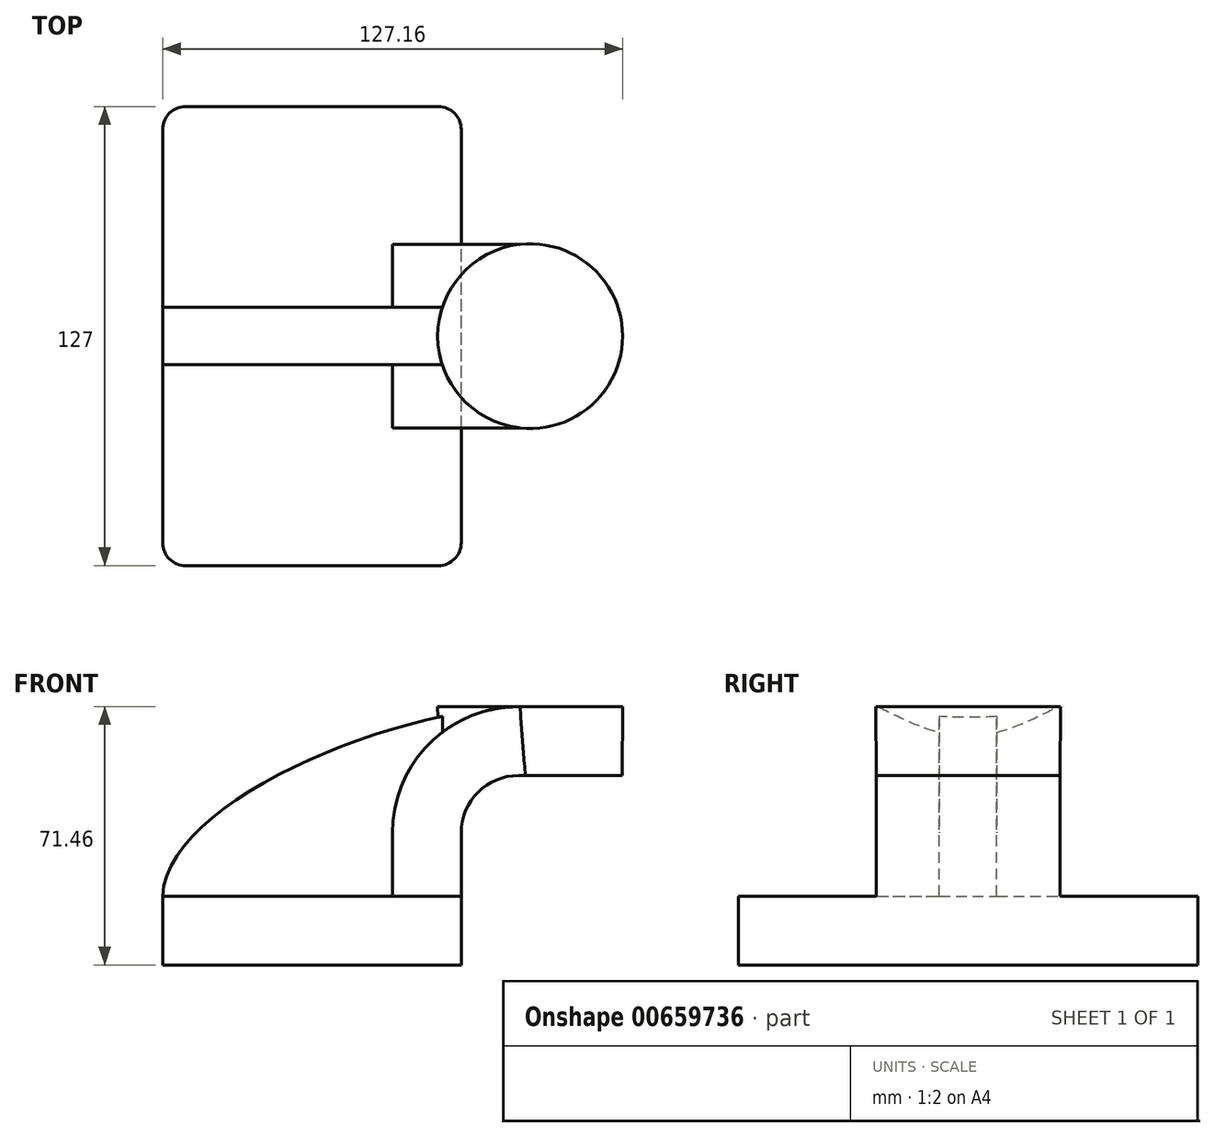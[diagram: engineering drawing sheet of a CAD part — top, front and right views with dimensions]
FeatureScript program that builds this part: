
annotation { "Feature Type Name" : "Feature", "Feature Type Description" : "" }
export const myFeature = defineFeature(function(context is Context, id is Id, definition is map)
    precondition{}
    {
        {
            var Q0;
            Q0=qCreatedBy(makeId("Front.planeOp"),FACE);
            var sketch = newSketch(context, id + "F0", { "sketchPlane" : qUnion([Q0])});
            skLineSegment(sketch, "E0.bottom", {"start": v(41.28, -9.52) * mm, "end": v(-41.28, -9.53) * mm});
            skLineSegment(sketch, "E0.top", {"start": v(41.28, 9.53) * mm, "end": v(-41.28, 9.53) * mm});
            skLineSegment(sketch, "E0.left", {"start": v(41.28, -9.52) * mm, "end": v(41.28, 9.53) * mm});
            skLineSegment(sketch, "E0.right", {"start": v(-41.28, -9.53) * mm, "end": v(-41.28, 9.53) * mm});
            skPoint(sketch, "E0.middle", {"position": v(0, 0) * mm});
            skLineSegment(sketch, "E1.bottom", {"start": v(111.12, 38.1) * mm, "end": v(60.32, 38.1) * mm});
            skLineSegment(sketch, "E1.top", {"start": v(111.12, 66.68) * mm, "end": v(60.32, 66.68) * mm});
            skLineSegment(sketch, "E1.left", {"start": v(111.12, 38.1) * mm, "end": v(111.12, 66.68) * mm});
            skLineSegment(sketch, "E1.right", {"start": v(60.32, 38.1) * mm, "end": v(60.32, 66.68) * mm});
            skPoint(sketch, "E1.middle", {"position": v(85.72, 52.39) * mm});
            skLineSegment(sketch, "E2", {"start": v(41.27, 9.53) * mm, "end": v(41.27, 27) * mm});
            skArc(sketch, "E3", {"start": v(41.27, 27) * mm, "mid": v(45.92, 38.23) * mm, "end": v(57.15, 42.88) * mm});
            skPoint(sketch, "E4.endSnap0", {"position": v(45.92, 38.23) * mm});
            skLineSegment(sketch, "E5", {"start": v(57.15, 42.88) * mm, "end": v(85.9, 42.88) * mm});
            skLineSegment(sketch, "E6.0", {"start": v(57.15, 61.93) * mm, "end": v(85.9, 61.93) * mm});
            skArc(sketch, "E6.1", {"start": v(22.23, 27) * mm, "mid": v(32.45, 51.7) * mm, "end": v(57.15, 61.93) * mm});
            skLineSegment(sketch, "E6.2", {"start": v(22.22, 9.53) * mm, "end": v(22.22, 27) * mm});
            skLineSegment(sketch, "E7", {"start": v(85.72, 38.1) * mm, "end": v(85.9, 66.68) * mm});
            skFitSpline(sketch, "E8", {"points": [v(-41.28, 9.52) * mm, v(57.15, 61.93) * mm], "startDerivative": vector(3.27, 78.83) * mm, "endDerivative": vector(107.24, 3.06) * mm});
            skSolve(sketch);
        }
        {
            var Q0;
            Q0=makeQuery(id+"F0.imprint","IMPRINT",FACE,{"disambiguationData":[TD([[makeQuery(id+"F0.imprint","IMPRINT",EDGE,{"derivedFrom":sQuery(id+"F0.wireOp",EDGE,"E0.bottom")}),-1.0]])]});
            extrude(context, id + "F1", {"entities" : qUnion([Q0]), "endBound" : BoundingType.SYMMETRIC, "depth" : 127 * mm, "offsetDistance" : 25.4 * mm});
        }
        {
            var Q0;
            {var subQ1=sQuery(id+"F0.wireOp",EDGE,"E2");Q0=makeQuery(id+"F0.imprint","IMPRINT",FACE,{"disambiguationData":[TD([[makeQuery(id+"F0.imprint","IMPRINT",EDGE,{"derivedFrom":subQ1}),1.0]])]});}
            extrude(context, id + "F2", {"entities" : qUnion([Q0]), "operationType" : NewBodyOperationType.ADD, "endBound" : BoundingType.SYMMETRIC, "depth" : 50.8 * mm, "offsetDistance" : 25.4 * mm});
        }
        {
            var Q0;
            {var subQ3=sQuery(id+"F0.wireOp",EDGE,"E6.2");Q0=makeQuery(id+"F0.imprint","IMPRINT",FACE,{"disambiguationData":[TD([[makeQuery(id+"F0.imprint","IMPRINT",EDGE,{"derivedFrom":subQ3}),1.0]])]});}
            extrude(context, id + "F3", {"entities" : qUnion([Q0]), "operationType" : NewBodyOperationType.ADD, "endBound" : BoundingType.SYMMETRIC, "depth" : 15.88 * mm, "offsetDistance" : 25.4 * mm});
        }
        {
            var Q0;
            Q0=makeQuery(id+"F1.opExtrude","CAP_EDGE",EDGE,{"disambiguationData":[OSD([sQuery(id+"F0.wireOp",EDGE,"E0.right")])],"isStart":false});
            var Q1;
            Q1=makeQuery(id+"F1.opExtrude","CAP_EDGE",EDGE,{"disambiguationData":[OSD([sQuery(id+"F0.wireOp",EDGE,"E0.left")])],"isStart":false});
            var Q2;
            Q2=makeQuery(id+"F1.opExtrude","CAP_EDGE",EDGE,{"disambiguationData":[OSD([sQuery(id+"F0.wireOp",EDGE,"E0.left")])],"isStart":true});
            var Q3;
            Q3=makeQuery(id+"F1.opExtrude","CAP_EDGE",EDGE,{"disambiguationData":[OSD([sQuery(id+"F0.wireOp",EDGE,"E0.right")])],"isStart":true});
            var Q4;
            Q4=makeQuery(id+"FM6gFoCJaelVOxE_1.opRevolve","SWEPT_FACE",FACE,{"disambiguationData":[OSD([sQuery(id+"F0.wireOp",EDGE,"E1.top")])]});
            fillet(context, id + "F4", {"entities" : qUnion([Q0, Q1, Q2, Q3, Q4]), "radius" : 6.35 * mm, "tangentPropagation" : true, "allowEdgeOverflow" : false});
        }
        {
            var Q0;
            {var subQ0=sQuery(id+"F0.wireOp",EDGE,"E5");var subQ1=sQuery(id+"F0.wireOp",EDGE,"E1.right");var subQ2=makeQuery(id+"F0.imprint","INTERSECT",VERTEX,{"derivedFrom":[subQ1,subQ0]});Q0=makeQuery(id+"F0.imprint","IMPRINT",FACE,{"disambiguationData":[TD([[makeQuery(id+"F0.imprint","IMPRINT",EDGE,{"disambiguationData":[TD([[subQ2,-1.0]])],"derivedFrom":subQ1}),-1.0]])]});}
            var Q1;
            Q1=sQuery(id+"F0.wireOp",EDGE,"E1.right");
            revolve(context, id + "F5", {"operationType" : NewBodyOperationType.ADD, "entities" : qUnion([Q0]), "axis" : qUnion([Q1]), "revolveType" : RevolveType.FULL});
        }
    });
